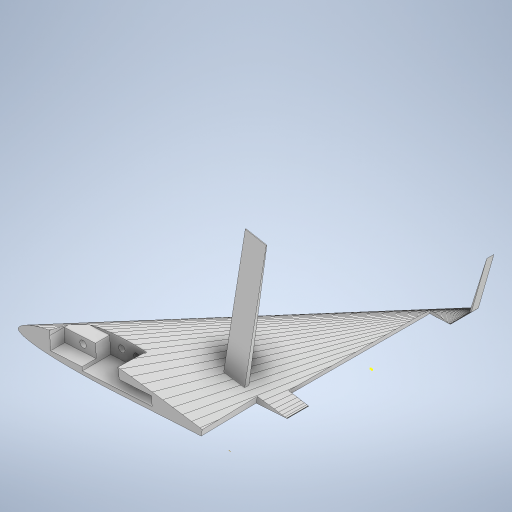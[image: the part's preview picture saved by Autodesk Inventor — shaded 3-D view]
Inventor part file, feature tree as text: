
AUTODESK INVENTOR PART (.ipt)
format: ipt  version: 2023 (Build 270158000, 158)  size: 932,864 bytes
history: native  units: mm
features: sketch x14, extrude x8, other x4, loft x2, hole x2
ambient origin geometry x8: Origin, YZ Plane, XZ Plane, XY Plane, X Axis, Y Axis, Z Axis, Center Point
bodies: Body1 (feature_tree), Body2 (feature_tree)
feature tree (30):
  sketch  "Szkic1"
  other  "Płaszczyzna konstrukcyjna2"
  loft  "Wyciągnięcie złożone2"
  other  "Płaszczyzna konstrukcyjna3"
  sketch  "Szkic7"
  extrude  "Wyciągnięcie proste2"  Depth=31.159588mm
  extrude  "Wyciągnięcie proste3"  Depth=1.516701mm
  extrude  "Wyciągnięcie proste4"  Depth=30.924079mm
  sketch  "Szkic11"
  other  "Płaszczyzna konstrukcyjna4"
  loft  "Wyciągnięcie złożone3"
  other  "Płaszczyzna konstrukcyjna5"
  sketch  "Szkic13"
  extrude  "Wyciągnięcie proste5"  Depth=30.873012mm
  sketch  "Szkic15"
  extrude  "Wyciągnięcie proste6"  Depth=29.561471mm
  extrude  "Wyciągnięcie proste7"  Depth=0.447545mm
  extrude  "Wyciągnięcie proste8"  Depth=29.600828mm
  extrude  "Wyciągnięcie proste9"  Depth=0.338663mm
  hole  "Otwór1"  [1 undecoded]
  hole  "Otwór2"  [1 undecoded]
  sketch  "Szkic6"
  sketch  "Szkic8"
  sketch  "Szkic9"
  sketch  "Szkic10"
  sketch  "Szkic12"
  sketch  "Szkic14"
  sketch  "Szkic16"
  sketch  "Szkic17"
  sketch  "Szkic18"
note: 2 required parameter values undecoded (feature->parameter linkage not recoverable at this tier; creation-order binding heuristic only, values carry confidence <= 0.55)
